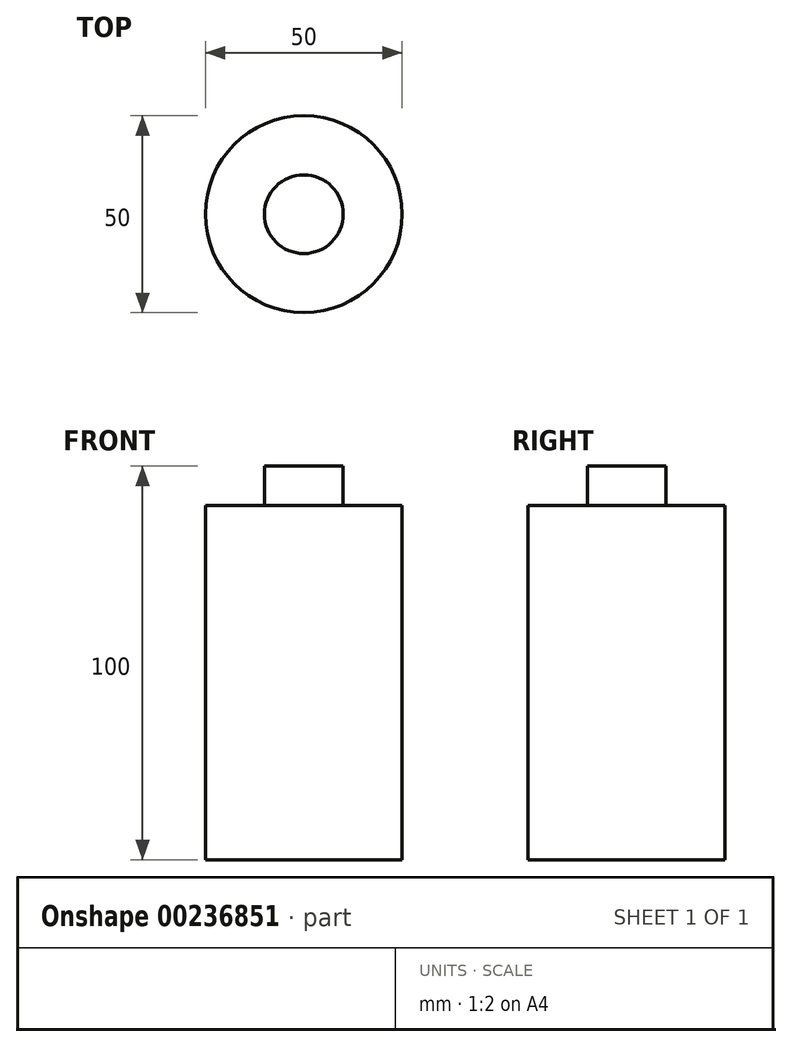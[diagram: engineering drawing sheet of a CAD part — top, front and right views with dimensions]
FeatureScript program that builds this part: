
annotation { "Feature Type Name" : "Feature", "Feature Type Description" : "" }
export const myFeature = defineFeature(function(context is Context, id is Id, definition is map)
    precondition{}
    {
        {
            var Q0;
            Q0=qCreatedBy(makeId("Front.planeOp"),FACE);
            var sketch = newSketch(context, id + "F0", { "sketchPlane" : qUnion([Q0])});
            skLineSegment(sketch, "E0", {"start": v(0, 65.7) * mm, "end": v(-10, 65.7) * mm});
            skLineSegment(sketch, "E1", {"start": v(-10, 65.7) * mm, "end": v(-10, 55.7) * mm});
            skLineSegment(sketch, "E2", {"start": v(-10, 55.7) * mm, "end": v(-25, 55.7) * mm});
            skLineSegment(sketch, "E3", {"start": v(-25, 55.7) * mm, "end": v(-25, -34.3) * mm});
            skLineSegment(sketch, "E4", {"start": v(-25, -34.3) * mm, "end": v(0, -34.3) * mm});
            skLineSegment(sketch, "E5", {"start": v(0, -34.3) * mm, "end": v(0, 65.7) * mm});
            skSolve(sketch);
        }
        {
            var Q0;
            Q0=makeQuery(id+"F0.imprint","IMPRINT",FACE,{"disambiguationData":[TD([[makeQuery(id+"F0.imprint","IMPRINT",EDGE,{"derivedFrom":sQuery(id+"F0.wireOp",EDGE,"E0")}),1.0]])]});
            var Q1;
            Q1=sQuery(id+"F0.wireOp",EDGE,"E5");
            revolve(context, id + "F1", {"entities" : qUnion([Q0]), "axis" : qUnion([Q1]), "revolveType" : RevolveType.FULL});
        }
        {
            var Q0;
            Q0=makeQuery(id+"F1.opRevolve","SWEPT_FACE",FACE,{"disambiguationData":[OSD([sQuery(id+"F0.wireOp",EDGE,"E0")])]});
            var sketch = newSketch(context, id + "F2", { "sketchPlane" : qUnion([Q0])});
            skCircle(sketch, "E6", {"center": v(0, 0) * mm, "radius": 6.36 * mm});
            skCircle(sketch, "E7", {"center": v(0, 0) * mm, "radius": 2.8 * mm});
            skSolve(sketch);
        }
        {
            var Q0;
            Q0=qCreatedBy(makeId("Front.planeOp"),FACE);
            var sketch = newSketch(context, id + "F3", { "sketchPlane" : qUnion([Q0])});
            skCircle(sketch, "E8", {"center": v(0, 0) * mm, "radius": 2.57 * mm});
            skSolve(sketch);
        }
        {
            var Q0;
            Q0 = qSketchRegion(id + "F3", true);
            var Q1;
            Q1 = qConstructionFilter(qBodyType(qCreatedBy(id + "F2" ,EDGE), BodyType.WIRE), ConstructionObject.NO);
            extrude(context, id + "F4", {"entities" : qUnion([Q0]), "bodyType" : ToolBodyType.SURFACE, "surfaceEntities" : qUnion([Q1]), "depth" : 25 * mm});
        }
    });
